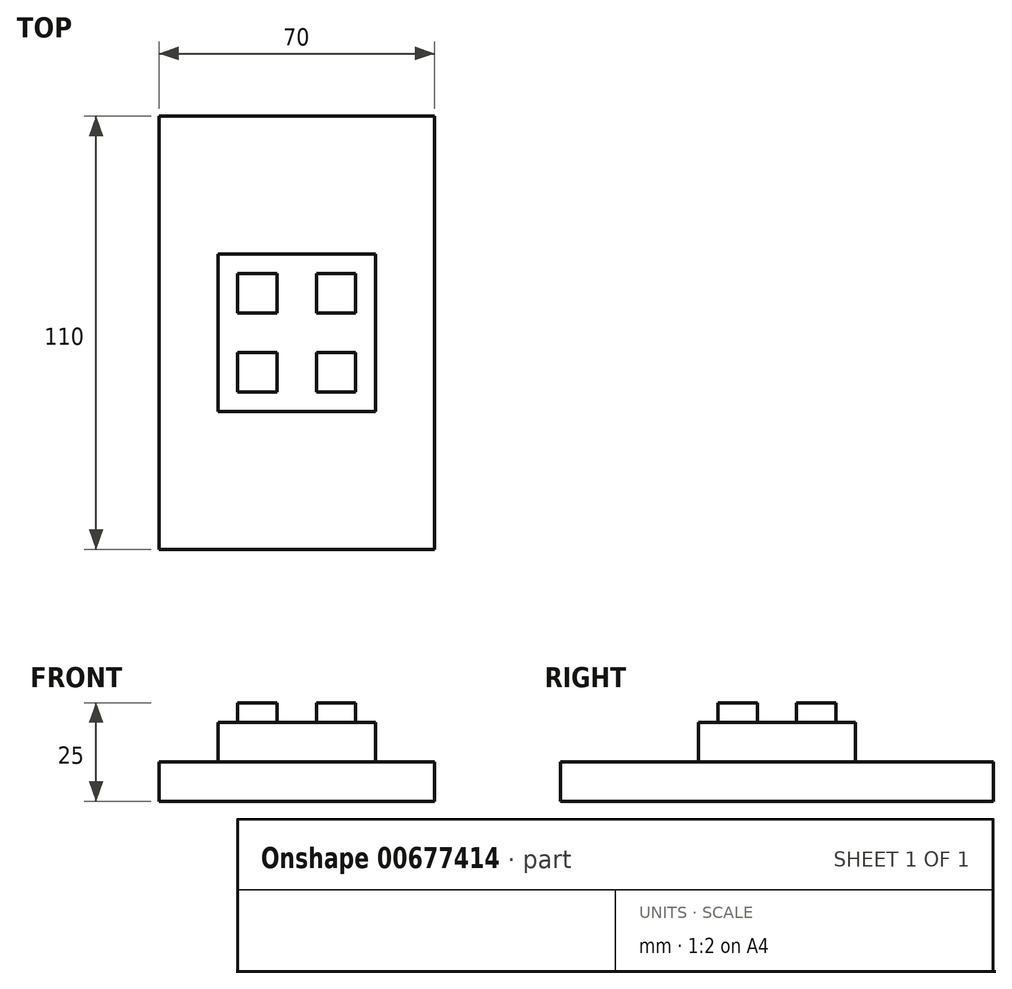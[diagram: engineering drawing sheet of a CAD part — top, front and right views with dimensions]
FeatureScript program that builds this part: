
annotation { "Feature Type Name" : "Feature", "Feature Type Description" : "" }
export const myFeature = defineFeature(function(context is Context, id is Id, definition is map)
    precondition{}
    {
        {
            var Q0;
            Q0=qCreatedBy(makeId("Top.planeOp"),FACE);
            var sketch = newSketch(context, id + "F0", { "sketchPlane" : qUnion([Q0])});
            skLineSegment(sketch, "E0.bottom", {"start": v(35, 55) * mm, "end": v(-35, 55) * mm});
            skLineSegment(sketch, "E0.top", {"start": v(35, -55) * mm, "end": v(-35, -55) * mm});
            skLineSegment(sketch, "E0.left", {"start": v(35, 55) * mm, "end": v(35, -55) * mm});
            skLineSegment(sketch, "E0.right", {"start": v(-35, 55) * mm, "end": v(-35, -55) * mm});
            skPoint(sketch, "E0.middle", {"position": v(0, 0) * mm});
            skPoint(sketch, "E1", {"position": v(0, -55) * mm});
            skSolve(sketch);
        }
        {
            var Q0;
            Q0=makeQuery(id+"F0.imprint","IMPRINT",FACE,{"disambiguationData":[TD([[makeQuery(id+"F0.imprint","IMPRINT",EDGE,{"derivedFrom":sQuery(id+"F0.wireOp",EDGE,"E0.bottom")}),1.0]])]});
            extrude(context, id + "F1", {"entities" : qUnion([Q0]), "depth" : 10 * mm, "offsetDistance" : 25 * mm});
        }
        {
            var Q0;
            Q0=makeQuery(id+"F1.opExtrude","CAP_FACE",FACE,{"disambiguationData":[OSD([sQuery(id+"F0.wireOp",EDGE,"E0.bottom"),sQuery(id+"F0.wireOp",EDGE,"E0.top"),sQuery(id+"F0.wireOp",EDGE,"E0.left"),sQuery(id+"F0.wireOp",EDGE,"E0.right")])],"isStart":false});
            var sketch = newSketch(context, id + "F2", { "sketchPlane" : qUnion([Q0])});
            skLineSegment(sketch, "E2.bottom", {"start": v(20, 20) * mm, "end": v(-20, 20) * mm});
            skLineSegment(sketch, "E2.top", {"start": v(20, -20) * mm, "end": v(-20, -20) * mm});
            skLineSegment(sketch, "E2.left", {"start": v(20, 20) * mm, "end": v(20, -20) * mm});
            skLineSegment(sketch, "E2.right", {"start": v(-20, 20) * mm, "end": v(-20, -20) * mm});
            skPoint(sketch, "E2.middle", {"position": v(0, 0) * mm});
            skSolve(sketch);
        }
        {
            var Q0;
            Q0=makeQuery(id+"F2.imprint","IMPRINT",FACE,{"disambiguationData":[TD([[makeQuery(id+"F2.imprint","IMPRINT",EDGE,{"derivedFrom":sQuery(id+"F2.wireOp",EDGE,"E2.bottom")}),1.0]])]});
            extrude(context, id + "F3", {"entities" : qUnion([Q0]), "operationType" : NewBodyOperationType.ADD, "depth" : 10 * mm, "offsetDistance" : 25 * mm});
        }
        {
            var Q0;
            Q0=makeQuery(id+"F3.opExtrude","CAP_FACE",FACE,{"disambiguationData":[OSD([sQuery(id+"F2.wireOp",EDGE,"E2.bottom"),sQuery(id+"F2.wireOp",EDGE,"E2.top"),sQuery(id+"F2.wireOp",EDGE,"E2.left"),sQuery(id+"F2.wireOp",EDGE,"E2.right")])],"isStart":false});
            var sketch = newSketch(context, id + "F4", { "sketchPlane" : qUnion([Q0])});
            skLineSegment(sketch, "E3.bottom", {"start": v(10, 10) * mm, "end": v(-10, 10) * mm, "construction": true});
            skLineSegment(sketch, "E3.top", {"start": v(10, -10) * mm, "end": v(-10, -10) * mm, "construction": true});
            skLineSegment(sketch, "E3.left", {"start": v(10, 10) * mm, "end": v(10, -10) * mm, "construction": true});
            skLineSegment(sketch, "E3.right", {"start": v(-10, 10) * mm, "end": v(-10, -10) * mm, "construction": true});
            skPoint(sketch, "E3.middle", {"position": v(0, 0) * mm});
            skLineSegment(sketch, "E4.bottom", {"start": v(-5, 15) * mm, "end": v(-15, 15) * mm});
            skLineSegment(sketch, "E4.top", {"start": v(-5, 5) * mm, "end": v(-15, 5) * mm});
            skLineSegment(sketch, "E4.left", {"start": v(-5, 15) * mm, "end": v(-5, 5) * mm});
            skLineSegment(sketch, "E4.right", {"start": v(-15, 15) * mm, "end": v(-15, 5) * mm});
            skPoint(sketch, "E4.middle", {"position": v(-10, 10) * mm});
            skLineSegment(sketch, "E5.bottom", {"start": v(15, 15) * mm, "end": v(5, 15) * mm});
            skLineSegment(sketch, "E5.top", {"start": v(15, 5) * mm, "end": v(5, 5) * mm});
            skLineSegment(sketch, "E5.left", {"start": v(15, 15) * mm, "end": v(15, 5) * mm});
            skLineSegment(sketch, "E5.right", {"start": v(5, 15) * mm, "end": v(5, 5) * mm});
            skPoint(sketch, "E5.middle", {"position": v(10, 10) * mm});
            skLineSegment(sketch, "E6.bottom", {"start": v(15, -5) * mm, "end": v(5, -5) * mm});
            skLineSegment(sketch, "E6.top", {"start": v(15, -15) * mm, "end": v(5, -15) * mm});
            skLineSegment(sketch, "E6.left", {"start": v(15, -5) * mm, "end": v(15, -15) * mm});
            skLineSegment(sketch, "E6.right", {"start": v(5, -5) * mm, "end": v(5, -15) * mm});
            skPoint(sketch, "E6.middle", {"position": v(10, -10) * mm});
            skLineSegment(sketch, "E7.bottom", {"start": v(-5, -5) * mm, "end": v(-15, -5) * mm});
            skLineSegment(sketch, "E7.top", {"start": v(-5, -15) * mm, "end": v(-15, -15) * mm});
            skLineSegment(sketch, "E7.left", {"start": v(-5, -5) * mm, "end": v(-5, -15) * mm});
            skLineSegment(sketch, "E7.right", {"start": v(-15, -5) * mm, "end": v(-15, -15) * mm});
            skPoint(sketch, "E7.middle", {"position": v(-10, -10) * mm});
            skSolve(sketch);
        }
        {
            var Q0;
            Q0=makeQuery(id+"F4.imprint","IMPRINT",FACE,{"disambiguationData":[TD([[makeQuery(id+"F4.imprint","IMPRINT",EDGE,{"derivedFrom":sQuery(id+"F4.wireOp",EDGE,"E4.bottom")}),1.0]])]});
            var Q1;
            Q1=makeQuery(id+"F4.imprint","IMPRINT",FACE,{"disambiguationData":[TD([[makeQuery(id+"F4.imprint","IMPRINT",EDGE,{"derivedFrom":sQuery(id+"F4.wireOp",EDGE,"E5.bottom")}),1.0]])]});
            var Q2;
            Q2=makeQuery(id+"F4.imprint","IMPRINT",FACE,{"disambiguationData":[TD([[makeQuery(id+"F4.imprint","IMPRINT",EDGE,{"derivedFrom":sQuery(id+"F4.wireOp",EDGE,"E6.bottom")}),1.0]])]});
            var Q3;
            Q3=makeQuery(id+"F4.imprint","IMPRINT",FACE,{"disambiguationData":[TD([[makeQuery(id+"F4.imprint","IMPRINT",EDGE,{"derivedFrom":sQuery(id+"F4.wireOp",EDGE,"E7.bottom")}),1.0]])]});
            extrude(context, id + "F5", {"entities" : qUnion([Q0, Q1, Q2, Q3]), "operationType" : NewBodyOperationType.ADD, "depth" : 5 * mm, "offsetDistance" : 25 * mm});
        }
    });
